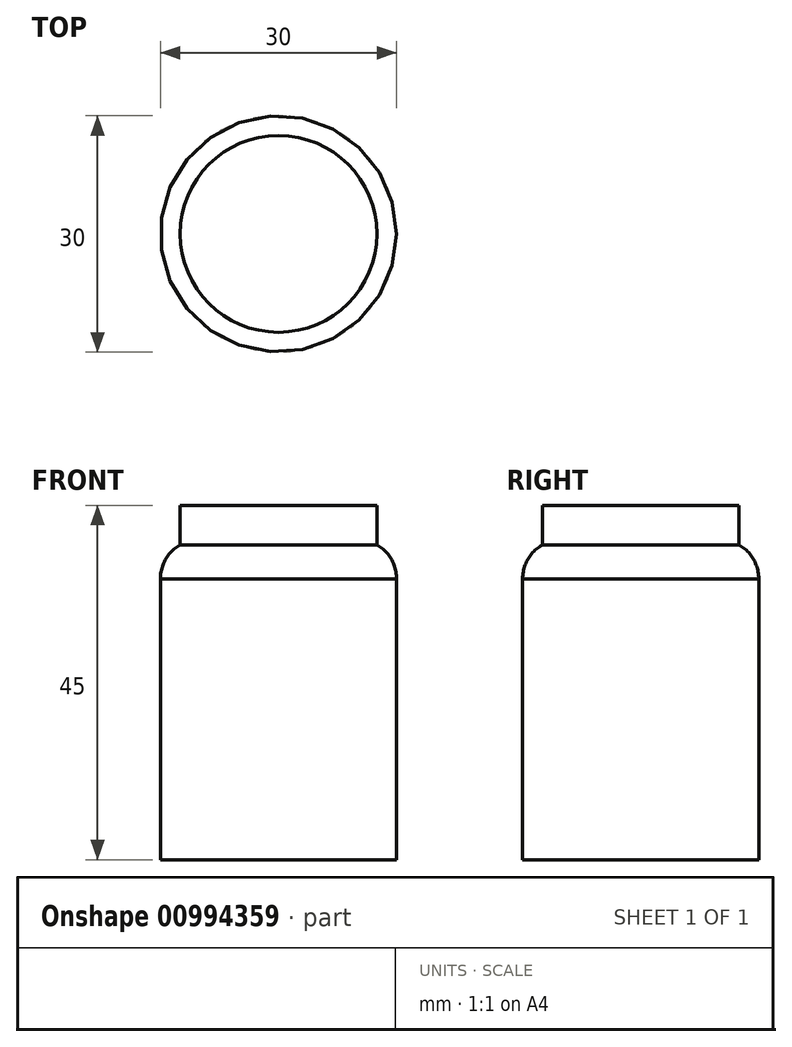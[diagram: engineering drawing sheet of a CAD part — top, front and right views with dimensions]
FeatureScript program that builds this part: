
annotation { "Feature Type Name" : "Feature", "Feature Type Description" : "" }
export const myFeature = defineFeature(function(context is Context, id is Id, definition is map)
    precondition{}
    {
        {
            var Q0;
            Q0=qCreatedBy(makeId("Top.planeOp"),FACE);
            var sketch = newSketch(context, id + "F0", { "sketchPlane" : qUnion([Q0])});
            skCircle(sketch, "E0", {"center": v(0, 30) * mm, "radius": 12.5 * mm});
            skSolve(sketch);
        }
        {
            var Q0;
            Q0=qCreatedBy(makeId("Top.planeOp"),FACE);
            var sketch = newSketch(context, id + "F1", { "sketchPlane" : qUnion([Q0])});
            skCircle(sketch, "E1", {"center": v(0, 30) * mm, "radius": 15 * mm});
            skSolve(sketch);
        }
        {
            var Q0;
            Q0 = qSketchRegion(id + "F0", true);
            extrude(context, id + "F2", {"entities" : qUnion([Q0]), "depth" : 45 * mm, "offsetDistance" : 25 * mm});
        }
        {
            var Q0;
            Q0 = qSketchRegion(id + "F0", true);
            var Q1;
            Q1 = qSketchRegion(id + "F1", true);
            extrude(context, id + "F3", {"entities" : qUnion([Q0, Q1]), "operationType" : NewBodyOperationType.ADD, "depth" : 40 * mm, "offsetDistance" : 25 * mm});
        }
        {
            var Q0;
            Q0=makeQuery(id+"F3.opExtrude","CAP_EDGE",EDGE,{"disambiguationData":[OSD([sQuery(id+"F1.wireOp",EDGE,"E1")])],"isStart":false});
            fillet(context, id + "F4", {"entities" : qUnion([Q0]), "radius" : 5 * mm, "tangentPropagation" : true, "allowEdgeOverflow" : false});
        }
    });
